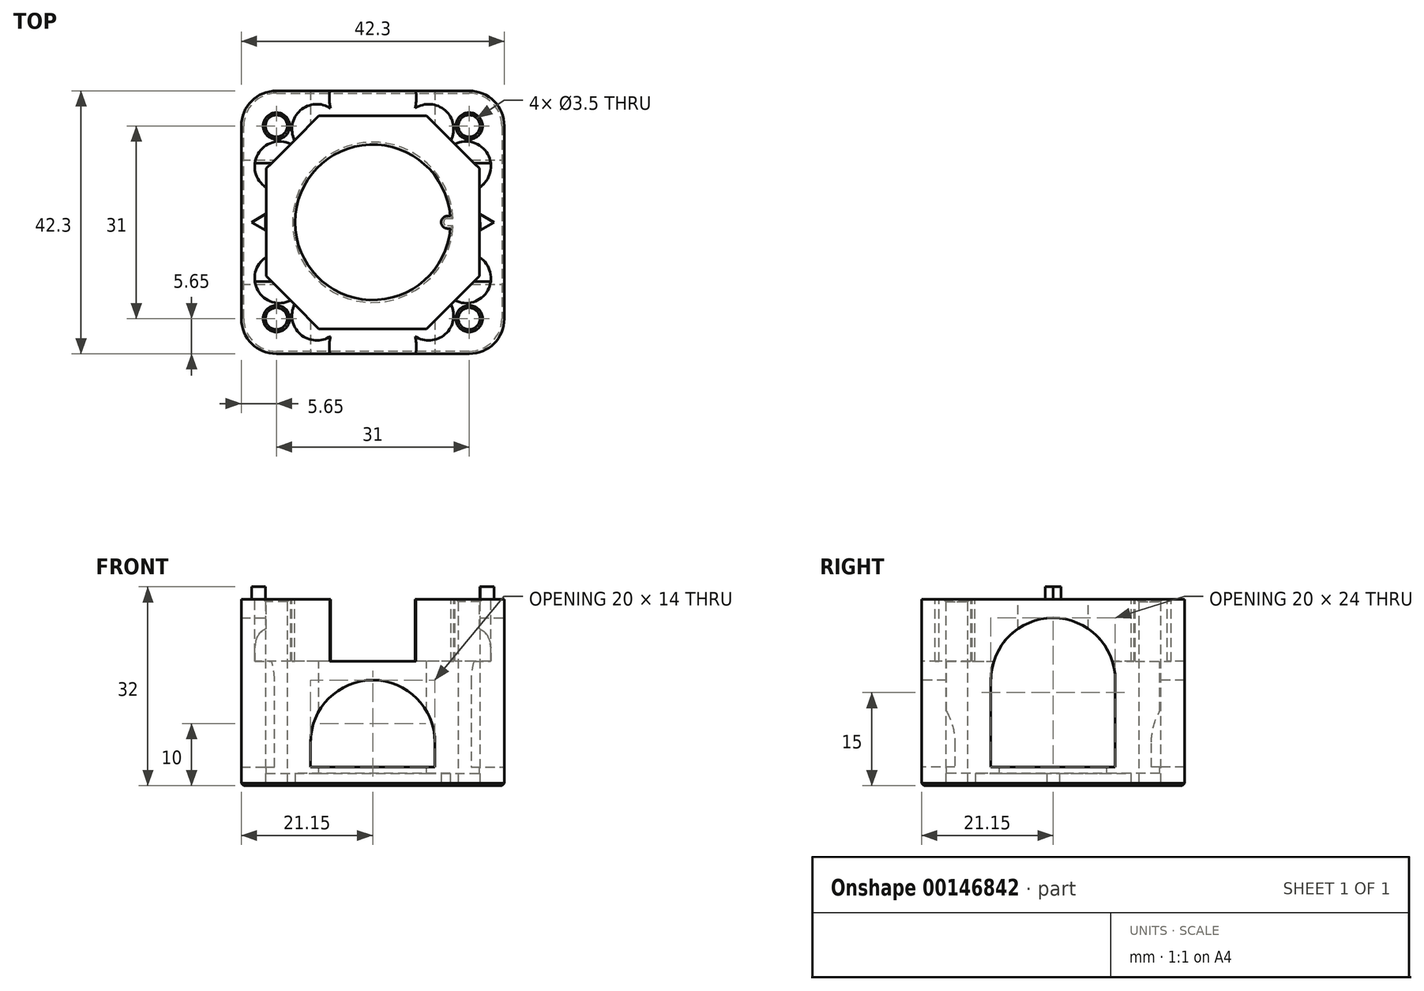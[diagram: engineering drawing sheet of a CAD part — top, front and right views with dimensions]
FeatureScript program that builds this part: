
annotation { "Feature Type Name" : "Feature", "Feature Type Description" : "" }
export const myFeature = defineFeature(function(context is Context, id is Id, definition is map)
    precondition{}
    {
        {
            var Q0;
            Q0=qCreatedBy(makeId("Top.planeOp"),FACE);
            var sketch = newSketch(context, id + "F0", { "sketchPlane" : qUnion([Q0])});
            skCircle(sketch, "E0", {"center": v(-15.5, 15.5) * mm, "radius": 1.75 * mm});
            skCircle(sketch, "E1", {"center": v(15.5, 15.5) * mm, "radius": 1.75 * mm});
            skCircle(sketch, "E2", {"center": v(15.5, -15.5) * mm, "radius": 1.75 * mm});
            skCircle(sketch, "E3", {"center": v(-15.5, -15.5) * mm, "radius": 1.75 * mm});
            skCircle(sketch, "E4", {"center": v(0, 0) * mm, "radius": 12.5 * mm});
            skLineSegment(sketch, "E5.bottom", {"start": v(15.5, 15.5) * mm, "end": v(-15.5, 15.5) * mm, "construction": true});
            skLineSegment(sketch, "E5.top", {"start": v(15.5, -15.5) * mm, "end": v(-15.5, -15.5) * mm, "construction": true});
            skLineSegment(sketch, "E5.left", {"start": v(15.5, 15.5) * mm, "end": v(15.5, -15.5) * mm, "construction": true});
            skLineSegment(sketch, "E5.right", {"start": v(-15.5, 15.5) * mm, "end": v(-15.5, -15.5) * mm, "construction": true});
            skLineSegment(sketch, "E6.bottom", {"start": v(-21.15, -21.15) * mm, "end": v(21.15, -21.15) * mm});
            skLineSegment(sketch, "E6.top", {"start": v(-21.15, 21.15) * mm, "end": v(21.15, 21.15) * mm});
            skLineSegment(sketch, "E6.left", {"start": v(-21.15, -21.15) * mm, "end": v(-21.15, 21.15) * mm});
            skLineSegment(sketch, "E6.right", {"start": v(21.15, -21.15) * mm, "end": v(21.15, 21.15) * mm});
            skSolve(sketch);
        }
        {
            var Q0;
            Q0=qSketchRegion(id+"F0",true);
            extrude(context, id + "F1", {"entities" : qUnion([Q0]), "depth" : 30 * mm});
        }
        {
            var Q0;
            Q0=qCreatedBy(makeId("Top.planeOp"),FACE);
            var sketch = newSketch(context, id + "F2", { "sketchPlane" : qUnion([Q0])});
            skArc(sketch, "E7", {"start": v(12, 1) * mm, "mid": v(11, 0) * mm, "end": v(12, -1) * mm});
            skLineSegment(sketch, "E8", {"start": v(12, 1) * mm, "end": v(13, 1) * mm});
            skLineSegment(sketch, "E9", {"start": v(13, 1) * mm, "end": v(13, -1) * mm});
            skLineSegment(sketch, "E10", {"start": v(13, -1) * mm, "end": v(12, -1) * mm});
            skSolve(sketch);
        }
        {
            var Q0;
            Q0=qSketchRegion(id+"F2",true);
            extrude(context, id + "F3", {"entities" : qUnion([Q0]), "operationType" : NewBodyOperationType.ADD, "depth" : 30 * mm});
        }
        {
            var Q0;
            {var subQ0=sQuery(id+"F2.wireOp",EDGE,"E10");var subQ1=sQuery(id+"F2.wireOp",EDGE,"E9");var subQ2=sQuery(id+"F2.wireOp",EDGE,"E8");var subQ3=sQuery(id+"F2.wireOp",EDGE,"E7");Q0=makeQuery(id+"FvvInixnSE8RDIe_1.11.F3.boolean.opBoolean","MERGE",FACE,{"derivedFrom":[makeQuery(id+"FvvInixnSE8RDIe_1.10.F3.boolean.opBoolean","MERGE",FACE,{"derivedFrom":[makeQuery(id+"FvvInixnSE8RDIe_1.9.F3.boolean.opBoolean","MERGE",FACE,{"derivedFrom":[makeQuery(id+"FvvInixnSE8RDIe_1.8.F3.boolean.opBoolean","MERGE",FACE,{"derivedFrom":[makeQuery(id+"FvvInixnSE8RDIe_1.7.F3.boolean.opBoolean","MERGE",FACE,{"derivedFrom":[makeQuery(id+"FvvInixnSE8RDIe_1.6.F3.boolean.opBoolean","MERGE",FACE,{"derivedFrom":[makeQuery(id+"FvvInixnSE8RDIe_1.5.F3.boolean.opBoolean","MERGE",FACE,{"derivedFrom":[makeQuery(id+"FvvInixnSE8RDIe_1.4.F3.boolean.opBoolean","MERGE",FACE,{"derivedFrom":[makeQuery(id+"FvvInixnSE8RDIe_1.3.F3.boolean.opBoolean","MERGE",FACE,{"derivedFrom":[makeQuery(id+"FvvInixnSE8RDIe_1.2.F3.boolean.opBoolean","MERGE",FACE,{"derivedFrom":[makeQuery(id+"FvvInixnSE8RDIe_1.1.F3.boolean.opBoolean","MERGE",FACE,{"derivedFrom":[makeQuery(id+"F3.boolean.opBoolean","MERGE",FACE,{"derivedFrom":[makeQuery(id+"F1.opExtrude","CAP_FACE",FACE,{"disambiguationData":[OSD([sQuery(id+"F0.wireOp",EDGE,"E0"),sQuery(id+"F0.wireOp",EDGE,"E1"),sQuery(id+"F0.wireOp",EDGE,"E2"),sQuery(id+"F0.wireOp",EDGE,"E3"),sQuery(id+"F0.wireOp",EDGE,"E4"),sQuery(id+"F0.wireOp",EDGE,"E6.bottom"),sQuery(id+"F0.wireOp",EDGE,"E6.top"),sQuery(id+"F0.wireOp",EDGE,"E6.left"),sQuery(id+"F0.wireOp",EDGE,"E6.right")])],"isStart":false}),makeQuery(id+"F3.opExtrude","CAP_FACE",FACE,{"disambiguationData":[OSD([subQ3,subQ2,subQ1,subQ0])],"isStart":false})]}),makeQuery(id+"FvvInixnSE8RDIe_1.1.F3.opExtrude","CAP_FACE",FACE,{"disambiguationData":[OSD([subQ3,subQ2,subQ1,subQ0])],"isStart":false})]}),makeQuery(id+"FvvInixnSE8RDIe_1.2.F3.opExtrude","CAP_FACE",FACE,{"disambiguationData":[OSD([subQ3,subQ2,subQ1,subQ0])],"isStart":false})]}),makeQuery(id+"FvvInixnSE8RDIe_1.3.F3.opExtrude","CAP_FACE",FACE,{"disambiguationData":[OSD([subQ3,subQ2,subQ1,subQ0])],"isStart":false})]}),makeQuery(id+"FvvInixnSE8RDIe_1.4.F3.opExtrude","CAP_FACE",FACE,{"disambiguationData":[OSD([subQ3,subQ2,subQ1,subQ0])],"isStart":false})]}),makeQuery(id+"FvvInixnSE8RDIe_1.5.F3.opExtrude","CAP_FACE",FACE,{"disambiguationData":[OSD([subQ3,subQ2,subQ1,subQ0])],"isStart":false})]}),makeQuery(id+"FvvInixnSE8RDIe_1.6.F3.opExtrude","CAP_FACE",FACE,{"disambiguationData":[OSD([subQ3,subQ2,subQ1,subQ0])],"isStart":false})]}),makeQuery(id+"FvvInixnSE8RDIe_1.7.F3.opExtrude","CAP_FACE",FACE,{"disambiguationData":[OSD([subQ3,subQ2,subQ1,subQ0])],"isStart":false})]}),makeQuery(id+"FvvInixnSE8RDIe_1.8.F3.opExtrude","CAP_FACE",FACE,{"disambiguationData":[OSD([subQ3,subQ2,subQ1,subQ0])],"isStart":false})]}),makeQuery(id+"FvvInixnSE8RDIe_1.9.F3.opExtrude","CAP_FACE",FACE,{"disambiguationData":[OSD([subQ3,subQ2,subQ1,subQ0])],"isStart":false})]}),makeQuery(id+"FvvInixnSE8RDIe_1.10.F3.opExtrude","CAP_FACE",FACE,{"disambiguationData":[OSD([subQ3,subQ2,subQ1,subQ0])],"isStart":false})]}),makeQuery(id+"FvvInixnSE8RDIe_1.11.F3.opExtrude","CAP_FACE",FACE,{"disambiguationData":[OSD([subQ3,subQ2,subQ1,subQ0])],"isStart":false})]});}
            var sketch = newSketch(context, id + "F4", { "sketchPlane" : qUnion([Q0])});
            skLineSegment(sketch, "E11.0", {"start": v(-17.15, 17.15) * mm, "end": v(17.15, 17.15) * mm});
            skLineSegment(sketch, "E11.1", {"start": v(-17.15, -17.15) * mm, "end": v(-17.15, 17.15) * mm});
            skLineSegment(sketch, "E11.2", {"start": v(-17.15, -17.15) * mm, "end": v(17.15, -17.15) * mm});
            skLineSegment(sketch, "E11.3", {"start": v(17.15, -17.15) * mm, "end": v(17.15, 17.15) * mm});
            skLineSegment(sketch, "E12", {"start": v(-17.15, 8.66) * mm, "end": v(-8.66, 17.15) * mm});
            skLineSegment(sketch, "E13", {"start": v(8.66, 17.15) * mm, "end": v(17.15, 8.66) * mm});
            skLineSegment(sketch, "E14", {"start": v(8.66, -17.15) * mm, "end": v(17.15, -8.66) * mm});
            skLineSegment(sketch, "E15", {"start": v(-17.15, -8.66) * mm, "end": v(-8.66, -17.15) * mm});
            skSolve(sketch);
        }
        {
            var Q0;
            {var subQ32=sQuery(id+"F4.wireOp",EDGE,"E12");Q0=makeQuery(id+"F4.imprint","IMPRINT",FACE,{"disambiguationData":[TD([[makeQuery(id+"F4.imprint","IMPRINT",EDGE,{"derivedFrom":subQ32}),-1.0]])]});}
            extrude(context, id + "F5", {"entities" : qUnion([Q0]), "operationType" : NewBodyOperationType.REMOVE, "oppositeDirection" : true, "depth" : 28 * mm});
        }
        {
            var Q0;
            {var subQ0=sQuery(id+"F2.wireOp",EDGE,"E10");var subQ1=sQuery(id+"F2.wireOp",EDGE,"E9");var subQ2=sQuery(id+"F2.wireOp",EDGE,"E8");var subQ3=sQuery(id+"F2.wireOp",EDGE,"E7");Q0=makeQuery(id+"FvvInixnSE8RDIe_1.11.F3.boolean.opBoolean","MERGE",FACE,{"derivedFrom":[makeQuery(id+"FvvInixnSE8RDIe_1.10.F3.boolean.opBoolean","MERGE",FACE,{"derivedFrom":[makeQuery(id+"FvvInixnSE8RDIe_1.9.F3.boolean.opBoolean","MERGE",FACE,{"derivedFrom":[makeQuery(id+"FvvInixnSE8RDIe_1.8.F3.boolean.opBoolean","MERGE",FACE,{"derivedFrom":[makeQuery(id+"FvvInixnSE8RDIe_1.7.F3.boolean.opBoolean","MERGE",FACE,{"derivedFrom":[makeQuery(id+"FvvInixnSE8RDIe_1.6.F3.boolean.opBoolean","MERGE",FACE,{"derivedFrom":[makeQuery(id+"FvvInixnSE8RDIe_1.5.F3.boolean.opBoolean","MERGE",FACE,{"derivedFrom":[makeQuery(id+"FvvInixnSE8RDIe_1.4.F3.boolean.opBoolean","MERGE",FACE,{"derivedFrom":[makeQuery(id+"FvvInixnSE8RDIe_1.3.F3.boolean.opBoolean","MERGE",FACE,{"derivedFrom":[makeQuery(id+"FvvInixnSE8RDIe_1.2.F3.boolean.opBoolean","MERGE",FACE,{"derivedFrom":[makeQuery(id+"FvvInixnSE8RDIe_1.1.F3.boolean.opBoolean","MERGE",FACE,{"derivedFrom":[makeQuery(id+"F3.boolean.opBoolean","MERGE",FACE,{"derivedFrom":[makeQuery(id+"F1.opExtrude","CAP_FACE",FACE,{"disambiguationData":[OSD([sQuery(id+"F0.wireOp",EDGE,"E0"),sQuery(id+"F0.wireOp",EDGE,"E1"),sQuery(id+"F0.wireOp",EDGE,"E2"),sQuery(id+"F0.wireOp",EDGE,"E3"),sQuery(id+"F0.wireOp",EDGE,"E4"),sQuery(id+"F0.wireOp",EDGE,"E6.bottom"),sQuery(id+"F0.wireOp",EDGE,"E6.top"),sQuery(id+"F0.wireOp",EDGE,"E6.left"),sQuery(id+"F0.wireOp",EDGE,"E6.right")])],"isStart":false}),makeQuery(id+"F3.opExtrude","CAP_FACE",FACE,{"disambiguationData":[OSD([subQ3,subQ2,subQ1,subQ0])],"isStart":false})]}),makeQuery(id+"FvvInixnSE8RDIe_1.1.F3.opExtrude","CAP_FACE",FACE,{"disambiguationData":[OSD([subQ3,subQ2,subQ1,subQ0])],"isStart":false})]}),makeQuery(id+"FvvInixnSE8RDIe_1.2.F3.opExtrude","CAP_FACE",FACE,{"disambiguationData":[OSD([subQ3,subQ2,subQ1,subQ0])],"isStart":false})]}),makeQuery(id+"FvvInixnSE8RDIe_1.3.F3.opExtrude","CAP_FACE",FACE,{"disambiguationData":[OSD([subQ3,subQ2,subQ1,subQ0])],"isStart":false})]}),makeQuery(id+"FvvInixnSE8RDIe_1.4.F3.opExtrude","CAP_FACE",FACE,{"disambiguationData":[OSD([subQ3,subQ2,subQ1,subQ0])],"isStart":false})]}),makeQuery(id+"FvvInixnSE8RDIe_1.5.F3.opExtrude","CAP_FACE",FACE,{"disambiguationData":[OSD([subQ3,subQ2,subQ1,subQ0])],"isStart":false})]}),makeQuery(id+"FvvInixnSE8RDIe_1.6.F3.opExtrude","CAP_FACE",FACE,{"disambiguationData":[OSD([subQ3,subQ2,subQ1,subQ0])],"isStart":false})]}),makeQuery(id+"FvvInixnSE8RDIe_1.7.F3.opExtrude","CAP_FACE",FACE,{"disambiguationData":[OSD([subQ3,subQ2,subQ1,subQ0])],"isStart":false})]}),makeQuery(id+"FvvInixnSE8RDIe_1.8.F3.opExtrude","CAP_FACE",FACE,{"disambiguationData":[OSD([subQ3,subQ2,subQ1,subQ0])],"isStart":false})]}),makeQuery(id+"FvvInixnSE8RDIe_1.9.F3.opExtrude","CAP_FACE",FACE,{"disambiguationData":[OSD([subQ3,subQ2,subQ1,subQ0])],"isStart":false})]}),makeQuery(id+"FvvInixnSE8RDIe_1.10.F3.opExtrude","CAP_FACE",FACE,{"disambiguationData":[OSD([subQ3,subQ2,subQ1,subQ0])],"isStart":false})]}),makeQuery(id+"FvvInixnSE8RDIe_1.11.F3.opExtrude","CAP_FACE",FACE,{"disambiguationData":[OSD([subQ3,subQ2,subQ1,subQ0])],"isStart":false})]});}
            var sketch = newSketch(context, id + "F6", { "sketchPlane" : qUnion([Q0])});
            skLineSegment(sketch, "E16.bottom", {"start": v(-9, 15) * mm, "end": v(9, 15) * mm, "construction": true});
            skLineSegment(sketch, "E16.top", {"start": v(-9, -15) * mm, "end": v(9, -15) * mm, "construction": true});
            skLineSegment(sketch, "E16.left", {"start": v(-9, 15) * mm, "end": v(-9, -15) * mm, "construction": true});
            skLineSegment(sketch, "E16.right", {"start": v(9, 15) * mm, "end": v(9, -15) * mm, "construction": true});
            skPoint(sketch, "E16.middle", {"position": v(0, 0) * mm});
            skCircle(sketch, "E17", {"center": v(-9, -15) * mm, "radius": 4 * mm});
            skCircle(sketch, "E18", {"center": v(-9, 15) * mm, "radius": 4 * mm});
            skCircle(sketch, "E19", {"center": v(9, 15) * mm, "radius": 4 * mm});
            skCircle(sketch, "E20", {"center": v(9, -15) * mm, "radius": 4 * mm});
            skLineSegment(sketch, "E21.bottom", {"start": v(-15, -9) * mm, "end": v(15, -9) * mm, "construction": true});
            skLineSegment(sketch, "E21.top", {"start": v(-15, 9) * mm, "end": v(15, 9) * mm, "construction": true});
            skLineSegment(sketch, "E21.left", {"start": v(-15, -9) * mm, "end": v(-15, 9) * mm, "construction": true});
            skLineSegment(sketch, "E21.right", {"start": v(15, -9) * mm, "end": v(15, 9) * mm, "construction": true});
            skCircle(sketch, "E22", {"center": v(-15, -9) * mm, "radius": 4 * mm});
            skCircle(sketch, "E23", {"center": v(-15, 9) * mm, "radius": 4 * mm});
            skCircle(sketch, "E24", {"center": v(15, 9) * mm, "radius": 4 * mm});
            skCircle(sketch, "E25", {"center": v(15, -9) * mm, "radius": 4 * mm});
            skLineSegment(sketch, "E26", {"start": v(0, -20) * mm, "end": v(0, 20) * mm, "construction": true});
            skCircle(sketch, "E27", {"center": v(0, -20) * mm, "radius": 7 * mm});
            skCircle(sketch, "E28", {"center": v(0, 20) * mm, "radius": 7 * mm});
            skSolve(sketch);
        }
        {
            var Q0;
            Q0=qSketchRegion(id+"F6",true);
            extrude(context, id + "F7", {"entities" : qUnion([Q0]), "operationType" : NewBodyOperationType.REMOVE, "oppositeDirection" : true, "depth" : 10 * mm});
        }
        {
            var Q0;
            {var subQ0=sQuery(id+"F0.wireOp",EDGE,"E3");var subQ1=sQuery(id+"F0.wireOp",EDGE,"E6.left");var subQ4=sQuery(id+"F0.wireOp",EDGE,"E6.top");var subQ5=sQuery(id+"F0.wireOp",EDGE,"E0");var subQ6=sQuery(id+"F0.wireOp",EDGE,"E6.bottom");var subQ15=sQuery(id+"F2.wireOp",EDGE,"E10");var subQ16=sQuery(id+"F2.wireOp",EDGE,"E9");var subQ17=sQuery(id+"F2.wireOp",EDGE,"E8");var subQ18=sQuery(id+"F2.wireOp",EDGE,"E7");Q0=makeQuery(id+"F7.boolean.opBoolean","SPLIT",FACE,{"disambiguationData":[TD([makeQuery(id+"F1.opExtrude","SWEPT_FACE",FACE,{"disambiguationData":[OSD([subQ5])]})])],"derivedFrom":makeQuery(id+"FvvInixnSE8RDIe_1.11.F3.boolean.opBoolean","MERGE",FACE,{"derivedFrom":[makeQuery(id+"FvvInixnSE8RDIe_1.10.F3.boolean.opBoolean","MERGE",FACE,{"derivedFrom":[makeQuery(id+"FvvInixnSE8RDIe_1.9.F3.boolean.opBoolean","MERGE",FACE,{"derivedFrom":[makeQuery(id+"FvvInixnSE8RDIe_1.8.F3.boolean.opBoolean","MERGE",FACE,{"derivedFrom":[makeQuery(id+"FvvInixnSE8RDIe_1.7.F3.boolean.opBoolean","MERGE",FACE,{"derivedFrom":[makeQuery(id+"FvvInixnSE8RDIe_1.6.F3.boolean.opBoolean","MERGE",FACE,{"derivedFrom":[makeQuery(id+"FvvInixnSE8RDIe_1.5.F3.boolean.opBoolean","MERGE",FACE,{"derivedFrom":[makeQuery(id+"FvvInixnSE8RDIe_1.4.F3.boolean.opBoolean","MERGE",FACE,{"derivedFrom":[makeQuery(id+"FvvInixnSE8RDIe_1.3.F3.boolean.opBoolean","MERGE",FACE,{"derivedFrom":[makeQuery(id+"FvvInixnSE8RDIe_1.2.F3.boolean.opBoolean","MERGE",FACE,{"derivedFrom":[makeQuery(id+"FvvInixnSE8RDIe_1.1.F3.boolean.opBoolean","MERGE",FACE,{"derivedFrom":[makeQuery(id+"F3.boolean.opBoolean","MERGE",FACE,{"derivedFrom":[makeQuery(id+"F1.opExtrude","CAP_FACE",FACE,{"disambiguationData":[OSD([subQ5,sQuery(id+"F0.wireOp",EDGE,"E1"),sQuery(id+"F0.wireOp",EDGE,"E2"),subQ0,sQuery(id+"F0.wireOp",EDGE,"E4"),subQ6,subQ4,subQ1,sQuery(id+"F0.wireOp",EDGE,"E6.right")])],"isStart":false}),makeQuery(id+"F3.opExtrude","CAP_FACE",FACE,{"disambiguationData":[OSD([subQ18,subQ17,subQ16,subQ15])],"isStart":false})]}),makeQuery(id+"FvvInixnSE8RDIe_1.1.F3.opExtrude","CAP_FACE",FACE,{"disambiguationData":[OSD([subQ18,subQ17,subQ16,subQ15])],"isStart":false})]}),makeQuery(id+"FvvInixnSE8RDIe_1.2.F3.opExtrude","CAP_FACE",FACE,{"disambiguationData":[OSD([subQ18,subQ17,subQ16,subQ15])],"isStart":false})]}),makeQuery(id+"FvvInixnSE8RDIe_1.3.F3.opExtrude","CAP_FACE",FACE,{"disambiguationData":[OSD([subQ18,subQ17,subQ16,subQ15])],"isStart":false})]}),makeQuery(id+"FvvInixnSE8RDIe_1.4.F3.opExtrude","CAP_FACE",FACE,{"disambiguationData":[OSD([subQ18,subQ17,subQ16,subQ15])],"isStart":false})]}),makeQuery(id+"FvvInixnSE8RDIe_1.5.F3.opExtrude","CAP_FACE",FACE,{"disambiguationData":[OSD([subQ18,subQ17,subQ16,subQ15])],"isStart":false})]}),makeQuery(id+"FvvInixnSE8RDIe_1.6.F3.opExtrude","CAP_FACE",FACE,{"disambiguationData":[OSD([subQ18,subQ17,subQ16,subQ15])],"isStart":false})]}),makeQuery(id+"FvvInixnSE8RDIe_1.7.F3.opExtrude","CAP_FACE",FACE,{"disambiguationData":[OSD([subQ18,subQ17,subQ16,subQ15])],"isStart":false})]}),makeQuery(id+"FvvInixnSE8RDIe_1.8.F3.opExtrude","CAP_FACE",FACE,{"disambiguationData":[OSD([subQ18,subQ17,subQ16,subQ15])],"isStart":false})]}),makeQuery(id+"FvvInixnSE8RDIe_1.9.F3.opExtrude","CAP_FACE",FACE,{"disambiguationData":[OSD([subQ18,subQ17,subQ16,subQ15])],"isStart":false})]}),makeQuery(id+"FvvInixnSE8RDIe_1.10.F3.opExtrude","CAP_FACE",FACE,{"disambiguationData":[OSD([subQ18,subQ17,subQ16,subQ15])],"isStart":false})]}),makeQuery(id+"FvvInixnSE8RDIe_1.11.F3.opExtrude","CAP_FACE",FACE,{"disambiguationData":[OSD([subQ18,subQ17,subQ16,subQ15])],"isStart":false})]})});}
            var sketch = newSketch(context, id + "F8", { "sketchPlane" : qUnion([Q0])});
            skLineSegment(sketch, "E29", {"start": v(-18, 0) * mm, "end": v(18, 0) * mm, "construction": true});
            skCircle(sketch, "E30.cCircle", {"center": v(-18, 0) * mm, "radius": 1.5 * mm, "construction": true});
            skLineSegment(sketch, "E30.0", {"start": v(-17.25, -1.3) * mm, "end": v(-19.5, 0) * mm});
            skLineSegment(sketch, "E30.1", {"start": v(-19.5, 0) * mm, "end": v(-17.25, 1.3) * mm});
            skLineSegment(sketch, "E30.2", {"start": v(-17.25, 1.3) * mm, "end": v(-17.25, -1.3) * mm});
            skCircle(sketch, "E31.cCircle", {"center": v(18, 0) * mm, "radius": 1.5 * mm, "construction": true});
            skLineSegment(sketch, "E31.0", {"start": v(17.25, 1.3) * mm, "end": v(19.5, 0) * mm});
            skLineSegment(sketch, "E31.1", {"start": v(19.5, 0) * mm, "end": v(17.25, -1.3) * mm});
            skLineSegment(sketch, "E31.2", {"start": v(17.25, -1.3) * mm, "end": v(17.25, 1.3) * mm});
            skSolve(sketch);
        }
        {
            var Q0;
            Q0=qSketchRegion(id+"F8",true);
            extrude(context, id + "F9", {"entities" : qUnion([Q0]), "operationType" : NewBodyOperationType.ADD, "depth" : 2 * mm});
        }
        {
            var Q0;
            Q0=makeQuery(id+"F1.opExtrude","SWEPT_FACE",FACE,{"disambiguationData":[OSD([sQuery(id+"F0.wireOp",EDGE,"E6.bottom")])]});
            var sketch = newSketch(context, id + "F10", { "sketchPlane" : qUnion([Q0])});
            skLineSegment(sketch, "E32", {"start": v(-10, 7) * mm, "end": v(-10, 3) * mm});
            skLineSegment(sketch, "E33", {"start": v(-10, 3) * mm, "end": v(10, 3) * mm});
            skLineSegment(sketch, "E34", {"start": v(10, 3) * mm, "end": v(10, 7) * mm});
            skArc(sketch, "E35", {"start": v(-10, 7) * mm, "mid": v(0, 17) * mm, "end": v(10, 7) * mm});
            skSolve(sketch);
        }
        {
            var Q0;
            Q0=qSketchRegion(id+"F10",true);
            extrude(context, id + "F11", {"entities" : qUnion([Q0]), "operationType" : NewBodyOperationType.REMOVE, "endBound" : BoundingType.THROUGH_ALL, "oppositeDirection" : true, "depth" : 25 * mm});
        }
        {
            var Q0;
            Q0=makeQuery(id+"F1.opExtrude","SWEPT_FACE",FACE,{"disambiguationData":[OSD([sQuery(id+"F0.wireOp",EDGE,"E6.right")])]});
            var sketch = newSketch(context, id + "F12", { "sketchPlane" : qUnion([Q0])});
            skLineSegment(sketch, "E36", {"start": v(-10, 17) * mm, "end": v(-10, 3) * mm});
            skLineSegment(sketch, "E37", {"start": v(-10, 3) * mm, "end": v(10, 3) * mm});
            skLineSegment(sketch, "E38", {"start": v(10, 3) * mm, "end": v(10, 17) * mm});
            skArc(sketch, "E39", {"start": v(-10, 17) * mm, "mid": v(0, 27) * mm, "end": v(10, 17) * mm});
            skSolve(sketch);
        }
        {
            var Q0;
            Q0=qSketchRegion(id+"F12",true);
            extrude(context, id + "F13", {"entities" : qUnion([Q0]), "operationType" : NewBodyOperationType.REMOVE, "endBound" : BoundingType.THROUGH_ALL, "oppositeDirection" : true, "depth" : 25 * mm});
        }
        {
            var Q0;
            Q0=makeQuery(id+"F1.opExtrude","SWEPT_EDGE",EDGE,{"disambiguationData":[OSD([sQuery(id+"F0.wireOp",EDGE,"E6.bottom"),sQuery(id+"F0.wireOp",EDGE,"E6.right")])]});
            var Q1;
            Q1=makeQuery(id+"F1.opExtrude","SWEPT_EDGE",EDGE,{"disambiguationData":[OSD([sQuery(id+"F0.wireOp",EDGE,"E6.top"),sQuery(id+"F0.wireOp",EDGE,"E6.right")])]});
            var Q2;
            Q2=makeQuery(id+"F1.opExtrude","SWEPT_EDGE",EDGE,{"disambiguationData":[OSD([sQuery(id+"F0.wireOp",EDGE,"E6.bottom"),sQuery(id+"F0.wireOp",EDGE,"E6.left")])]});
            var Q3;
            Q3=makeQuery(id+"F1.opExtrude","SWEPT_EDGE",EDGE,{"disambiguationData":[OSD([sQuery(id+"F0.wireOp",EDGE,"E6.top"),sQuery(id+"F0.wireOp",EDGE,"E6.left")])]});
            fillet(context, id + "F14", {"entities" : qUnion([Q0, Q1, Q2, Q3]), "radius" : 5.65 * mm, "tangentPropagation" : true, "allowEdgeOverflow" : false});
        }
        {
            var Q0;
            {var subQ0=sQuery(id+"F2.wireOp",EDGE,"E10");var subQ1=sQuery(id+"F2.wireOp",EDGE,"E9");var subQ2=sQuery(id+"F2.wireOp",EDGE,"E8");var subQ3=sQuery(id+"F2.wireOp",EDGE,"E7");Q0=makeQuery(id+"FvvInixnSE8RDIe_1.11.F3.boolean.opBoolean","MERGE",FACE,{"derivedFrom":[makeQuery(id+"FvvInixnSE8RDIe_1.10.F3.boolean.opBoolean","MERGE",FACE,{"derivedFrom":[makeQuery(id+"FvvInixnSE8RDIe_1.9.F3.boolean.opBoolean","MERGE",FACE,{"derivedFrom":[makeQuery(id+"FvvInixnSE8RDIe_1.8.F3.boolean.opBoolean","MERGE",FACE,{"derivedFrom":[makeQuery(id+"FvvInixnSE8RDIe_1.7.F3.boolean.opBoolean","MERGE",FACE,{"derivedFrom":[makeQuery(id+"FvvInixnSE8RDIe_1.6.F3.boolean.opBoolean","MERGE",FACE,{"derivedFrom":[makeQuery(id+"FvvInixnSE8RDIe_1.5.F3.boolean.opBoolean","MERGE",FACE,{"derivedFrom":[makeQuery(id+"FvvInixnSE8RDIe_1.4.F3.boolean.opBoolean","MERGE",FACE,{"derivedFrom":[makeQuery(id+"FvvInixnSE8RDIe_1.3.F3.boolean.opBoolean","MERGE",FACE,{"derivedFrom":[makeQuery(id+"FvvInixnSE8RDIe_1.2.F3.boolean.opBoolean","MERGE",FACE,{"derivedFrom":[makeQuery(id+"FvvInixnSE8RDIe_1.1.F3.boolean.opBoolean","MERGE",FACE,{"derivedFrom":[makeQuery(id+"F3.boolean.opBoolean","MERGE",FACE,{"derivedFrom":[makeQuery(id+"F1.opExtrude","CAP_FACE",FACE,{"disambiguationData":[OSD([sQuery(id+"F0.wireOp",EDGE,"E0"),sQuery(id+"F0.wireOp",EDGE,"E1"),sQuery(id+"F0.wireOp",EDGE,"E2"),sQuery(id+"F0.wireOp",EDGE,"E3"),sQuery(id+"F0.wireOp",EDGE,"E4"),sQuery(id+"F0.wireOp",EDGE,"E6.bottom"),sQuery(id+"F0.wireOp",EDGE,"E6.top"),sQuery(id+"F0.wireOp",EDGE,"E6.left"),sQuery(id+"F0.wireOp",EDGE,"E6.right")])],"isStart":true}),makeQuery(id+"F3.opExtrude","CAP_FACE",FACE,{"disambiguationData":[OSD([subQ3,subQ2,subQ1,subQ0])],"isStart":true})]}),makeQuery(id+"FvvInixnSE8RDIe_1.1.F3.opExtrude","CAP_FACE",FACE,{"disambiguationData":[OSD([subQ3,subQ2,subQ1,subQ0])],"isStart":true})]}),makeQuery(id+"FvvInixnSE8RDIe_1.2.F3.opExtrude","CAP_FACE",FACE,{"disambiguationData":[OSD([subQ3,subQ2,subQ1,subQ0])],"isStart":true})]}),makeQuery(id+"FvvInixnSE8RDIe_1.3.F3.opExtrude","CAP_FACE",FACE,{"disambiguationData":[OSD([subQ3,subQ2,subQ1,subQ0])],"isStart":true})]}),makeQuery(id+"FvvInixnSE8RDIe_1.4.F3.opExtrude","CAP_FACE",FACE,{"disambiguationData":[OSD([subQ3,subQ2,subQ1,subQ0])],"isStart":true})]}),makeQuery(id+"FvvInixnSE8RDIe_1.5.F3.opExtrude","CAP_FACE",FACE,{"disambiguationData":[OSD([subQ3,subQ2,subQ1,subQ0])],"isStart":true})]}),makeQuery(id+"FvvInixnSE8RDIe_1.6.F3.opExtrude","CAP_FACE",FACE,{"disambiguationData":[OSD([subQ3,subQ2,subQ1,subQ0])],"isStart":true})]}),makeQuery(id+"FvvInixnSE8RDIe_1.7.F3.opExtrude","CAP_FACE",FACE,{"disambiguationData":[OSD([subQ3,subQ2,subQ1,subQ0])],"isStart":true})]}),makeQuery(id+"FvvInixnSE8RDIe_1.8.F3.opExtrude","CAP_FACE",FACE,{"disambiguationData":[OSD([subQ3,subQ2,subQ1,subQ0])],"isStart":true})]}),makeQuery(id+"FvvInixnSE8RDIe_1.9.F3.opExtrude","CAP_FACE",FACE,{"disambiguationData":[OSD([subQ3,subQ2,subQ1,subQ0])],"isStart":true})]}),makeQuery(id+"FvvInixnSE8RDIe_1.10.F3.opExtrude","CAP_FACE",FACE,{"disambiguationData":[OSD([subQ3,subQ2,subQ1,subQ0])],"isStart":true})]}),makeQuery(id+"FvvInixnSE8RDIe_1.11.F3.opExtrude","CAP_FACE",FACE,{"disambiguationData":[OSD([subQ3,subQ2,subQ1,subQ0])],"isStart":true})]});}
            chamfer(context, id + "F15", {"entities" : qUnion([Q0]), "width" : 0.4 * mm, "tangentPropagation" : true});
        }
        {
            var Q0;
            Q0=makeQuery(id+"F1.opExtrude","CAP_EDGE",EDGE,{"disambiguationData":[OSD([sQuery(id+"F0.wireOp",EDGE,"E0")])],"isStart":false});
            var Q1;
            Q1=makeQuery(id+"F1.opExtrude","CAP_EDGE",EDGE,{"disambiguationData":[OSD([sQuery(id+"F0.wireOp",EDGE,"E3")])],"isStart":false});
            var Q2;
            Q2=makeQuery(id+"F1.opExtrude","CAP_EDGE",EDGE,{"disambiguationData":[OSD([sQuery(id+"F0.wireOp",EDGE,"E1")])],"isStart":false});
            var Q3;
            Q3=makeQuery(id+"F1.opExtrude","CAP_EDGE",EDGE,{"disambiguationData":[OSD([sQuery(id+"F0.wireOp",EDGE,"E2")])],"isStart":false});
            chamfer(context, id + "F16", {"entities" : qUnion([Q0, Q1, Q2, Q3]), "width" : 0.4 * mm, "tangentPropagation" : true});
        }
    });
